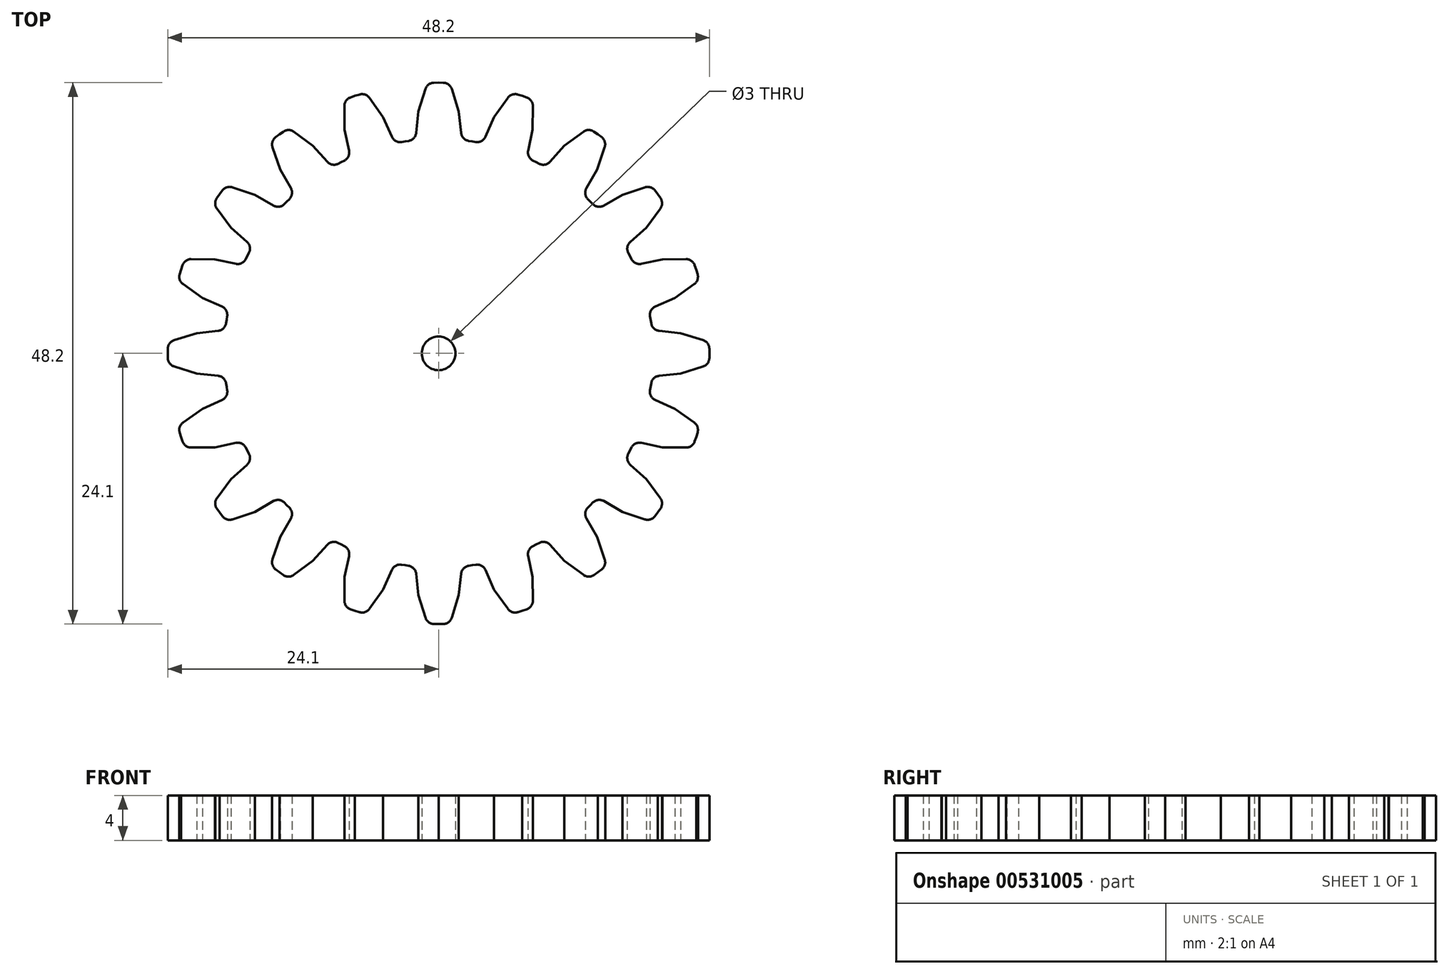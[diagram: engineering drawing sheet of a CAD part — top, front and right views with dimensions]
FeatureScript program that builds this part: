
annotation { "Feature Type Name" : "Feature", "Feature Type Description" : "" }
export const myFeature = defineFeature(function(context is Context, id is Id, definition is map)
    precondition{}
    {
        {
            assignVariable(context, id + "F0", {"name" : "nzuba", "anyValue" : 20});
        }
        {
            var Q0;
            Q0=qCreatedBy(makeId("Front.planeOp"),FACE);
            var sketch = newSketch(context, id + "F1", { "sketchPlane" : qUnion([Q0])});
            skLineSegment(sketch, "E0", {"start": v(0, 0) * mm, "end": v(0, 4) * mm, "construction": true});
            skSolve(sketch);
        }
        {
            var Q0;
            Q0=qCreatedBy(makeId("Top.planeOp"),FACE);
            var sketch = newSketch(context, id + "F2", { "sketchPlane" : qUnion([Q0])});
            skArc(sketch, "E1", {"start": v(18.86, 3) * mm, "mid": v(-19.1, 0) * mm, "end": v(18.86, -3) * mm});
            skCircle(sketch, "E2", {"center": v(0, 0) * mm, "radius": 24.1 * mm, "construction": true});
            skCircle(sketch, "E3", {"center": v(0, 0) * mm, "radius": 21.6 * mm, "construction": true});
            skLineSegment(sketch, "E4", {"start": v(0, 19.1) * mm, "end": v(0, 24.1) * mm, "construction": true});
            skLineSegment(sketch, "E5", {"start": v(-3.68, 23.82) * mm, "end": v(-3.3, 21.35) * mm, "construction": true});
            skLineSegment(sketch, "E6", {"start": v(-3.3, 21.35) * mm, "end": v(-2.92, 18.87) * mm, "construction": true});
            skLineSegment(sketch, "E7", {"start": v(0, 0) * mm, "end": v(24.1, 0) * mm, "construction": true});
            skLineSegment(sketch, "E8", {"start": v(0, 0) * mm, "end": v(18.86, 3) * mm});
            skLineSegment(sketch, "E9", {"start": v(0, 0) * mm, "end": v(19.62, 2) * mm, "construction": true});
            skPoint(sketch, "E10", {"position": v(19, 1.94) * mm});
            skLineSegment(sketch, "E11", {"start": v(19.62, 2) * mm, "end": v(21.52, 1.8) * mm});
            skLineSegment(sketch, "E12", {"start": v(21.52, 1.8) * mm, "end": v(23.53, 1.17) * mm});
            skLineSegment(sketch, "E13", {"start": v(24.09, 0.43) * mm, "end": v(24.1, 0) * mm});
            skPoint(sketch, "E14.visualSharp", {"position": v(24.08, 1) * mm});
            skArc(sketch, "E14.filletArc", {"start": v(24.09, 0.43) * mm, "mid": v(23.93, 0.89) * mm, "end": v(23.53, 1.17) * mm});
            skLineSegment(sketch, "E15.MirrorCS", {"start": v(19.62, -2) * mm, "end": v(21.52, -1.8) * mm});
            skLineSegment(sketch, "E16.MirrorCS", {"start": v(21.52, -1.8) * mm, "end": v(23.53, -1.17) * mm});
            skArc(sketch, "E17.MirrorCS", {"start": v(24.09, -0.43) * mm, "mid": v(23.93, -0.89) * mm, "end": v(23.53, -1.17) * mm});
            skLineSegment(sketch, "E18.MirrorCS", {"start": v(24.09, -0.43) * mm, "end": v(24.1, 0) * mm});
            skLineSegment(sketch, "E19.MirrorCS", {"start": v(0, 0) * mm, "end": v(18.86, -3) * mm});
            skCircle(sketch, "E20", {"center": v(0, 0) * mm, "radius": 1.5 * mm});
            skLineSegment(sketch, "E21", {"start": v(18.86, 3) * mm, "end": v(18.91, 2.67) * mm});
            skArc(sketch, "E22", {"start": v(18.91, 2.67) * mm, "mid": v(19.15, 2.22) * mm, "end": v(19.62, 2) * mm});
            skLineSegment(sketch, "E23.MirrorCS", {"start": v(18.86, -3) * mm, "end": v(18.91, -2.67) * mm});
            skArc(sketch, "E24.MirrorCS", {"start": v(18.91, -2.67) * mm, "mid": v(19.15, -2.22) * mm, "end": v(19.62, -2) * mm});
            skSolve(sketch);
        }
        {
            var Q0;
            Q0=makeQuery(id+"F2.imprint","IMPRINT",FACE,{"disambiguationData":[TD([[makeQuery(id+"F2.imprint","IMPRINT",EDGE,{"derivedFrom":sQuery(id+"F2.wireOp",EDGE,"E11")}),-1.0]])]});
            extrude(context, id + "F3", {"entities" : qUnion([Q0]), "depth" : 4 * mm, "offsetDistance" : 25 * mm});
        }
        {
            var Q0;
            Q0=makeQuery(id+"F3.opExtrude","SWEPT_BODY",BODY,{"disambiguationData":[OSD([sQuery(id+"F2.wireOp",EDGE,"E8"),sQuery(id+"F2.wireOp",EDGE,"Ccr5RPwP-yEiI-mMhH-aCbI-xiKkbVCYuAfT"),sQuery(id+"F2.wireOp",EDGE,"E11"),sQuery(id+"F2.wireOp",EDGE,"E12"),sQuery(id+"F2.wireOp",EDGE,"E13"),sQuery(id+"F2.wireOp",EDGE,"E14.filletArc"),sQuery(id+"F2.wireOp",EDGE,"434113d8-d490-4e0a-a8ba-07c452dbb1c90.MirrorCS"),sQuery(id+"F2.wireOp",EDGE,"E15.MirrorCS"),sQuery(id+"F2.wireOp",EDGE,"E16.MirrorCS"),sQuery(id+"F2.wireOp",EDGE,"E17.MirrorCS"),sQuery(id+"F2.wireOp",EDGE,"E18.MirrorCS"),sQuery(id+"F2.wireOp",EDGE,"E19.MirrorCS")])]});
            var Q1;
            Q1=sQuery(id+"F1.wireOp",EDGE,"E0");
            circularPattern(context, id + "F4", {"operationType" : NewBodyOperationType.ADD, "entities" : qUnion([Q0]), "axis" : qUnion([Q1]), "angle" : 360 * degree, "instanceCount" : getVariable(context, 'nzuba'), "equalSpace" : true, "computeTransformsWithoutBuiltin" : true});
        }
    });
